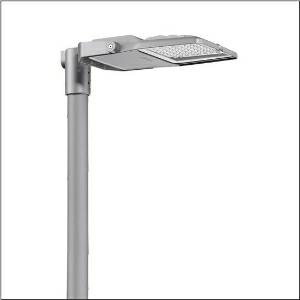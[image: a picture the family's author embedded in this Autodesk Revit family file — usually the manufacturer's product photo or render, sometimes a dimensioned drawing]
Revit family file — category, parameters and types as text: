
# Revit family: floodlight_fl_21_mini___pl43_5xa7771c2a3a_40a9
name_source: partatom
category: Lighting Fixtures
units: mm (PartAtom-declared; Revit-internal decimal feet)

## family parameters
Cut with Voids When Loaded = No
Host = Face
Light Source = No
Part Type = Normal
Room Calculation Point = No
Round Connector Dimension = Use Diameter
Shared = No

## types (1)
- --- (1 x LED, 12520 lm, 87.2 W, 3000K)
    Apparent Load = 87 VA
    CIE Flux Codes = 27 78 99 100 100
    Color Rendering = 70
    Color Temperature = 3000K
    Default Elevation = 1800 mm
    Description = Floodlight FL 21 mini, floodlight, primary light control with lens, of PMMA, primary optical cover: protective disc, of toughened safety glass, transparent, light distribution: PL43, light emission: direct distribution, installation type: surface-mounted, LED, High Power LED, rated luminous flux: 12.520lm, luminous efficacy: 144lm/W, light colour: 730, colour temperature: 3000K, control gear: ECG iQ, control: Auto-Match, Temp-Guard, Lumen-Switch, Night-Set, Smart-Wire, Light-Fading, Desk-Remote (wireless, voltage-free reading and setting of iQ features in the workshop via application-optimized NFC function/RFID function), optimised constant luminous flux control (CLO 2.0), with terminal, 6-pole, mains connection: 220..240V, AC, 50/60Hz, start of lifetime: 87W, end of lifetime: 92W, reduction: 40W, luminaire housing, of diecast aluminium, powder-coated, Siteco® metallic grey (DB 702S), corrosivity category C5 according to DIN EN ISO 12944, mast bracket, of steel, galvanised, powder-coated, Siteco® metallic grey (DB 702S), protection rating (complete): IP66, insulation class (complete): insulation class II (safety insulation), certification: CE, ENEC, VDE, protection symbol: D, impact resistance: IK08, permissible operating ambient temperature: -40..+40°C, permissible operating ambient temperature for outdoor applications: -40..+50°C, standard: DIN EN 12944, packaging unit: 1 piece

Light Distribution: PL43
    Height = 70 mm
    Lamp = 1 x LED
    Lamp Light Flux = 12520 lm
    Lamp Power = 87.2 W
    Lamp count = 1
    Length = 485 mm
    Luminous efficacy = 144 lm/W
    Manufacturer = Siteco
    ModVariant = No
    Model = 5XA7771C2A3A
    Number of Poles = 1
    OnlyDefault = Yes
    Power Factor = 1
    Product Name = Floodlight FL 21 mini | PL43
    Product group = floodlight | pylon top
    ProductGroupID = 6101
    Protection Class = Protection class II
    Protection Degree = IP 66
    RLX_Detail_Level = 1
    RlxData = <blob elided: 101077 chars, md5=a26e6c88>
    Socket = socket
    Standby Power = 0 W
    System Light Flux = 12520 lm
    System Power = 87 W
    Type Comments = factory setting: luminous flux: 100 % | dim-lin: 254 | 456 mA
    Type Image = l_1007125.jpg
    URL = http://relux.com
    VarID = @adj_073689
    Voltage = 0 V
    Weight = 0.00 kg
    Width = 337 mm

## geometry (parser evidence)
native form markers: Blend x4, Sweep x13
no freeform markers — native parametric forms only
